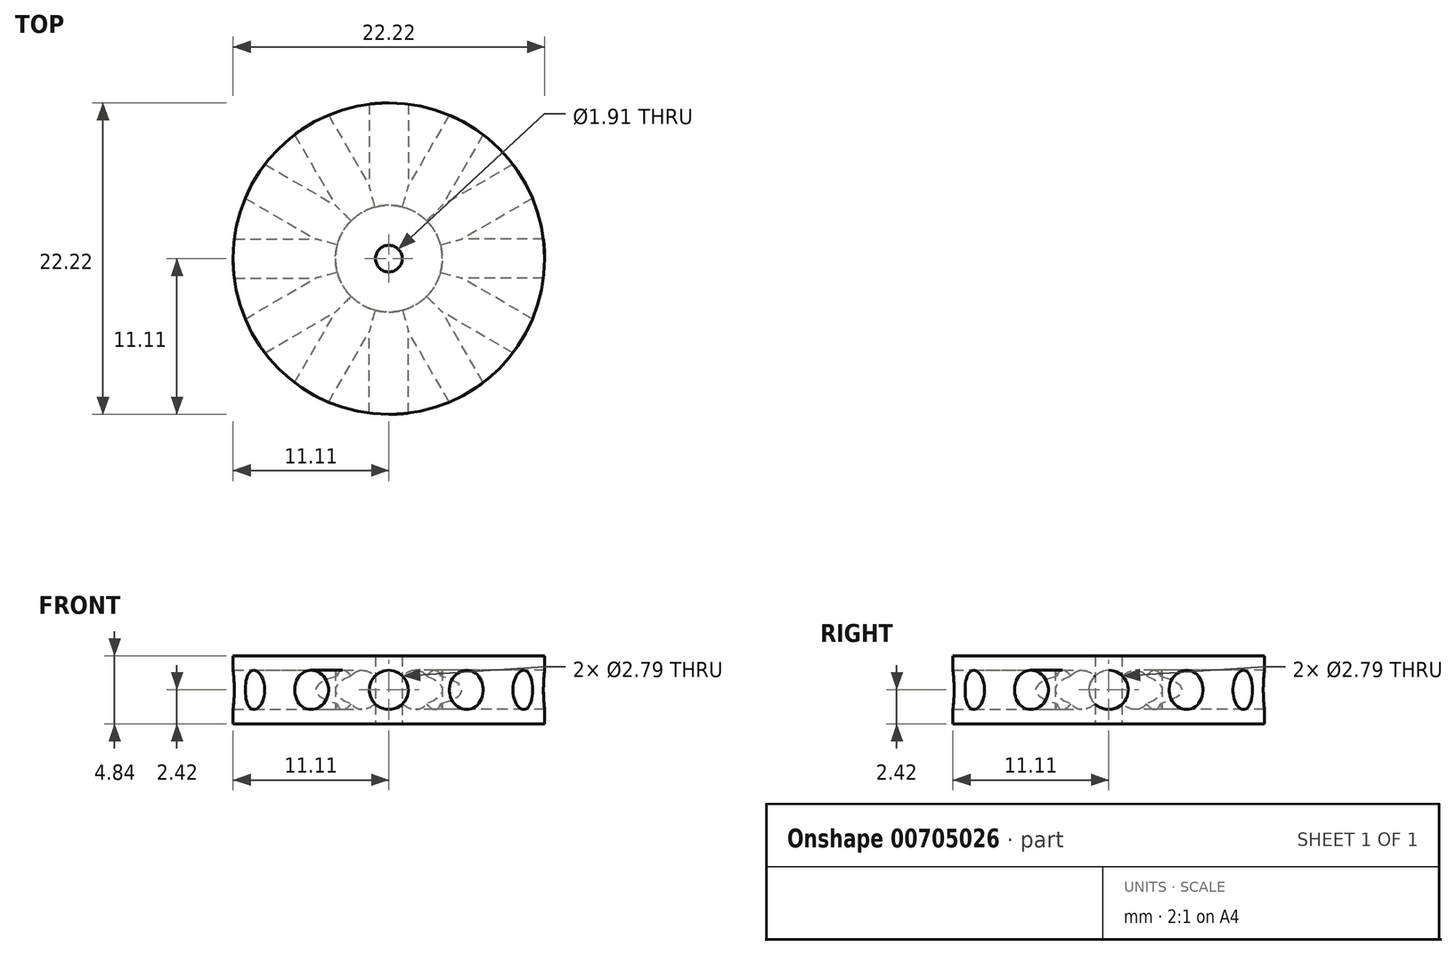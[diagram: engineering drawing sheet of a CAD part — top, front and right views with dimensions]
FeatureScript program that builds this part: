
annotation { "Feature Type Name" : "Feature", "Feature Type Description" : "" }
export const myFeature = defineFeature(function(context is Context, id is Id, definition is map)
    precondition{}
    {
        {
            var Q0;
            Q0=qCreatedBy(makeId("Top.planeOp"),FACE);
            var sketch = newSketch(context, id + "F0", { "sketchPlane" : qUnion([Q0])});
            skCircle(sketch, "E0", {"center": v(0, 0) * mm, "radius": 11.11 * mm});
            skCircle(sketch, "E1", {"center": v(0, 0) * mm, "radius": 0.95 * mm});
            skLineSegment(sketch, "E2", {"start": v(0, 0) * mm, "end": v(16.02, 0) * mm, "construction": true});
            skLineSegment(sketch, "E3.1.0", {"start": v(0, 0) * mm, "end": v(-8.01, 13.88) * mm, "construction": true});
            skLineSegment(sketch, "E3.2.0", {"start": v(0, 0) * mm, "end": v(-8.01, -13.88) * mm, "construction": true});
            skLineSegment(sketch, "E4.1.0", {"start": v(0, 0) * mm, "end": v(0, 16.02) * mm, "construction": true});
            skLineSegment(sketch, "E4.2.0", {"start": v(0, 0) * mm, "end": v(-16.02, 0) * mm, "construction": true});
            skLineSegment(sketch, "E4.3.0", {"start": v(0, 0) * mm, "end": v(0, -16.02) * mm, "construction": true});
            skSolve(sketch);
        }
        {
            var Q0;
            Q0=makeQuery(id+"F0.imprint","IMPRINT",FACE,{"disambiguationData":[TD([[makeQuery(id+"F0.imprint","IMPRINT",EDGE,{"derivedFrom":sQuery(id+"F0.wireOp",EDGE,"E0")}),1.0]])]});
            extrude(context, id + "F1", {"entities" : qUnion([Q0]), "depth" : 4.84 * mm, "offsetDistance" : 25.4 * mm, "symmetric" : true});
        }
        {
            var Q0;
            Q0=qCreatedBy(makeId("Right.planeOp"),FACE);
            var sketch = newSketch(context, id + "F2", { "sketchPlane" : qUnion([Q0])});
            skCircle(sketch, "E5", {"center": v(0, 0) * mm, "radius": 1.75 * mm, "construction": true});
            skCircle(sketch, "E6", {"center": v(0, 0) * mm, "radius": 1.4 * mm});
            skSolve(sketch);
        }
        {
            var Q0;
            Q0=qSketchRegion(id+"F2",true);
            var Q1;
            Q1=makeQuery(id+"F1.opExtrude","SWEPT_FACE",FACE,{"disambiguationData":[OSD([sQuery(id+"F0.wireOp",EDGE,"E0")])]});
            extrude(context, id + "F3", {"entities" : qUnion([Q0]), "endBound" : BoundingType.UP_TO_SURFACE, "depth" : 25.4 * mm, "endBoundEntityFace" : qUnion([Q1]), "offsetDistance" : 25.4 * mm});
        }
        {
            var Q0;
            Q0=qCreatedBy(makeId("Front.planeOp"),FACE);
            var sketch = newSketch(context, id + "F4", { "sketchPlane" : qUnion([Q0])});
            skLineSegment(sketch, "E7", {"start": v(0, 0) * mm, "end": v(0, 5.7) * mm, "construction": true});
            skSolve(sketch);
        }
        {
            var Q0;
            Q0=makeQuery(id+"F3.opExtrude","SWEPT_BODY",BODY,{"disambiguationData":[OSD([sQuery(id+"F2.wireOp",EDGE,"E6")])]});
            var Q1;
            Q1=sQuery(id+"F4.wireOp",EDGE,"E7");
            circularPattern(context, id + "F5", {"operationType" : NewBodyOperationType.REMOVE, "entities" : qUnion([Q0]), "axis" : qUnion([Q1]), "angle" : 360 * degree, "instanceCount" : 12, "equalSpace" : true});
        }
        {
            var Q0;
            Q0=qCreatedBy(makeId("Top.planeOp"),FACE);
            var sketch = newSketch(context, id + "F6", { "sketchPlane" : qUnion([Q0])});
            skCircle(sketch, "E8", {"center": v(0, 0) * mm, "radius": 3.81 * mm});
            skCircle(sketch, "E9.0", {"center": v(0, 0) * mm, "radius": 0.95 * mm});
            skSolve(sketch);
        }
        {
            var Q0;
            Q0=qSketchRegion(id+"F6",true);
            var Q1;
            Q1=makeQuery(id+"F1.opExtrude","CAP_FACE",FACE,{"disambiguationData":[OSD([sQuery(id+"F0.wireOp",EDGE,"E0"),sQuery(id+"F0.wireOp",EDGE,"E1")])],"isStart":false});
            var Q2;
            Q2=makeQuery(id+"F1.opExtrude","CAP_FACE",FACE,{"disambiguationData":[OSD([sQuery(id+"F0.wireOp",EDGE,"E0"),sQuery(id+"F0.wireOp",EDGE,"E1")])],"isStart":true});
            extrude(context, id + "F7", {"entities" : qUnion([Q0]), "operationType" : NewBodyOperationType.ADD, "endBound" : BoundingType.UP_TO_SURFACE, "depth" : 25.4 * mm, "endBoundEntityFace" : qUnion([Q1]), "offsetDistance" : 25.4 * mm, "hasSecondDirection" : true, "secondDirectionBound" : BoundingType.UP_TO_SURFACE, "secondDirectionOppositeDirection" : true, "secondDirectionDepth" : 25.4 * mm, "secondDirectionBoundEntityFace" : qUnion([Q2])});
        }
    });
